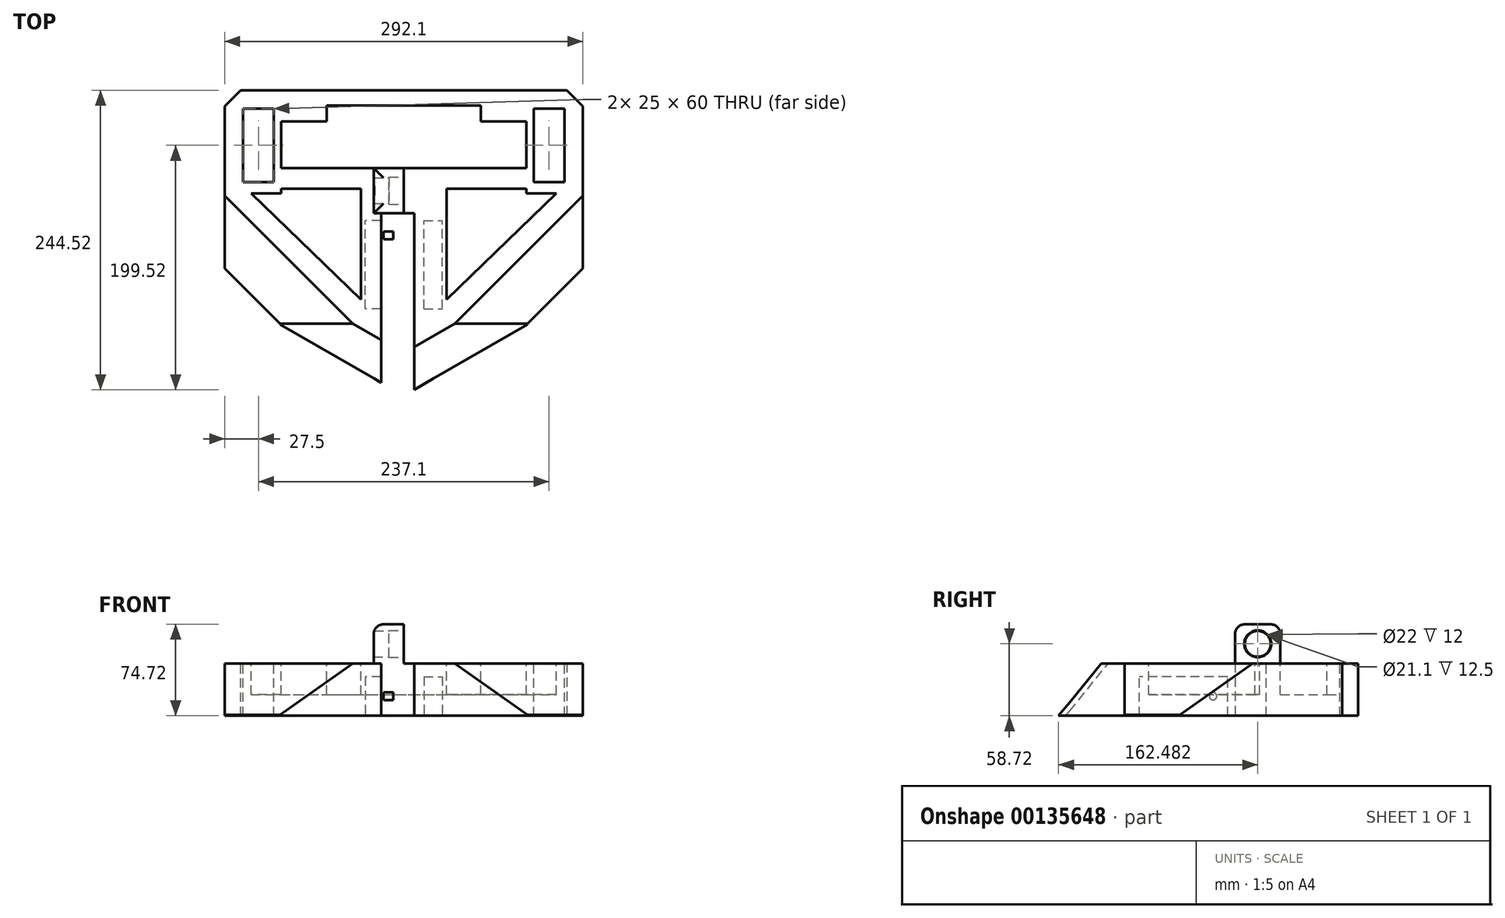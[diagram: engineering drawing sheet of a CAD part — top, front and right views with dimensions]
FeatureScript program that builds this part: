
annotation { "Feature Type Name" : "Feature", "Feature Type Description" : "" }
export const myFeature = defineFeature(function(context is Context, id is Id, definition is map)
    precondition{}
    {
        {
            var Q0;
            Q0=qCreatedBy(makeId("Top.planeOp"),FACE);
            var sketch = newSketch(context, id + "F0", { "sketchPlane" : qUnion([Q0])});
            skLineSegment(sketch, "E0.bottom", {"start": v(-146.05, -95.25) * mm, "end": v(146.05, -95.25) * mm});
            skLineSegment(sketch, "E0.top", {"start": v(-146.05, 95.25) * mm, "end": v(146.05, 95.25) * mm});
            skLineSegment(sketch, "E0.left", {"start": v(-146.05, -95.25) * mm, "end": v(-146.05, 95.25) * mm});
            skLineSegment(sketch, "E0.right", {"start": v(146.05, -95.25) * mm, "end": v(146.05, 95.25) * mm});
            skPoint(sketch, "E0.middle", {"position": v(0, 0) * mm});
            skLineSegment(sketch, "E1", {"start": v(0, -95.25) * mm, "end": v(0, 95.25) * mm, "construction": true});
            skLineSegment(sketch, "E2", {"start": v(0, -5.25) * mm, "end": v(-8.5, -5.25) * mm});
            skLineSegment(sketch, "E3", {"start": v(-8.5, -5.25) * mm, "end": v(-8.5, -95.25) * mm});
            skLineSegment(sketch, "E4.MirrorCS", {"start": v(0, -5.25) * mm, "end": v(8.5, -5.25) * mm});
            skLineSegment(sketch, "E5.MirrorCS", {"start": v(8.5, -5.25) * mm, "end": v(8.5, -95.25) * mm});
            skSolve(sketch);
        }
        {
            var Q0;
            Q0=makeQuery(id+"F0.imprint","IMPRINT",FACE,{"disambiguationData":[TD([[makeQuery(id+"F0.imprint","IMPRINT",EDGE,{"derivedFrom":sQuery(id+"F0.wireOp",EDGE,"E0.bottom")}),1.0]])]});
            extrude(context, id + "F1", {"entities" : qUnion([Q0]), "depth" : 42.72 * mm});
        }
        {
            var Q0;
            Q0=makeQuery(id+"F1.opExtrude","CAP_FACE",FACE,{"disambiguationData":[OSD([sQuery(id+"F0.wireOp",EDGE,"E0.bottom"),sQuery(id+"F0.wireOp",EDGE,"E0.top"),sQuery(id+"F0.wireOp",EDGE,"E0.left"),sQuery(id+"F0.wireOp",EDGE,"E0.right")])],"isStart":false});
            var sketch = newSketch(context, id + "F2", { "sketchPlane" : qUnion([Q0])});
            skLineSegment(sketch, "E6.bottom", {"start": v(-131.05, 80.25) * mm, "end": v(-106.05, 80.25) * mm});
            skLineSegment(sketch, "E6.top", {"start": v(-131.05, 20.25) * mm, "end": v(-106.05, 20.25) * mm});
            skLineSegment(sketch, "E6.left", {"start": v(-131.05, 80.25) * mm, "end": v(-131.05, 20.25) * mm});
            skLineSegment(sketch, "E6.right", {"start": v(-106.05, 80.25) * mm, "end": v(-106.05, 20.25) * mm});
            skLineSegment(sketch, "E7.MirrorCS", {"start": v(106.05, 80.25) * mm, "end": v(106.05, 20.25) * mm});
            skLineSegment(sketch, "E8.MirrorCS", {"start": v(131.05, 80.25) * mm, "end": v(131.05, 20.25) * mm});
            skLineSegment(sketch, "E9.MirrorCS", {"start": v(131.05, 20.25) * mm, "end": v(106.05, 20.25) * mm});
            skLineSegment(sketch, "E10.MirrorCS", {"start": v(131.05, 80.25) * mm, "end": v(106.05, 80.25) * mm});
            skSolve(sketch);
        }
        {
            var Q0;
            Q0=makeQuery(id+"F2.imprint","IMPRINT",FACE,{"disambiguationData":[TD([[makeQuery(id+"F2.imprint","IMPRINT",EDGE,{"derivedFrom":sQuery(id+"F2.wireOp",EDGE,"E6.bottom")}),-1.0]])]});
            var Q1;
            Q1=makeQuery(id+"F2.imprint","IMPRINT",FACE,{"disambiguationData":[TD([[makeQuery(id+"F2.imprint","IMPRINT",EDGE,{"derivedFrom":sQuery(id+"F2.wireOp",EDGE,"2fe5a682-8a8e-47e5-9a97-2ca4f21bb82e0.MirrorCS")}),1.0]])]});
            var Q2;
            Q2=makeQuery(id+"F2.imprint","IMPRINT",FACE,{"disambiguationData":[TD([[makeQuery(id+"F2.imprint","IMPRINT",EDGE,{"derivedFrom":sQuery(id+"F2.wireOp",EDGE,"E7.MirrorCS")}),1.0]])]});
            extrude(context, id + "F3", {"entities" : qUnion([Q0, Q1, Q2]), "operationType" : NewBodyOperationType.REMOVE, "oppositeDirection" : true, "depth" : 500 * mm});
        }
        {
            var Q0;
            Q0=makeQuery(id+"F1.opExtrude","CAP_FACE",FACE,{"disambiguationData":[OSD([sQuery(id+"F0.wireOp",EDGE,"E0.bottom"),sQuery(id+"F0.wireOp",EDGE,"E0.top"),sQuery(id+"F0.wireOp",EDGE,"E0.left"),sQuery(id+"F0.wireOp",EDGE,"E0.right")])],"isStart":false});
            var sketch = newSketch(context, id + "F4", { "sketchPlane" : qUnion([Q0])});
            skLineSegment(sketch, "E11.bottom", {"start": v(-100.05, 31.67) * mm, "end": v(100.05, 31.67) * mm});
            skLineSegment(sketch, "E11.top", {"start": v(-100.05, 69.67) * mm, "end": v(-62.8, 69.67) * mm});
            skLineSegment(sketch, "E11.left", {"start": v(-100.05, 31.67) * mm, "end": v(-100.05, 69.67) * mm});
            skLineSegment(sketch, "E11.right", {"start": v(100.05, 31.67) * mm, "end": v(100.05, 69.67) * mm});
            skPoint(sketch, "E11.middle", {"position": v(0, 50.67) * mm});
            skLineSegment(sketch, "E12.top", {"start": v(-62.8, 82.87) * mm, "end": v(62.8, 82.87) * mm});
            skLineSegment(sketch, "E12.left", {"start": v(-62.8, 69.67) * mm, "end": v(-62.8, 82.87) * mm});
            skLineSegment(sketch, "E12.right", {"start": v(62.8, 69.67) * mm, "end": v(62.8, 82.87) * mm});
            skPoint(sketch, "E12.middle", {"position": v(0, 69.67) * mm});
            skPoint(sketch, "E12.bottom.start.orphan", {"position": v(-62.8, 56.48) * mm});
            skLineSegment(sketch, "E13.trimOffspring", {"start": v(62.8, 69.67) * mm, "end": v(100.05, 69.67) * mm});
            skPoint(sketch, "E14.orphan", {"position": v(62.8, 56.48) * mm});
            skLineSegment(sketch, "E15", {"start": v(-106.05, 50.25) * mm, "end": v(106.05, 50.67) * mm, "construction": true});
            skPoint(sketch, "E15.endSnap0", {"position": v(-100.05, 50.67) * mm});
            skLineSegment(sketch, "E16", {"start": v(-100.05, 31.67) * mm, "end": v(-100.05, 10.92) * mm});
            skLineSegment(sketch, "E17", {"start": v(-100.05, 10.92) * mm, "end": v(-124.52, 10.92) * mm});
            skLineSegment(sketch, "E18", {"start": v(-124.52, 10.92) * mm, "end": v(-34.99, -75.74) * mm});
            skLineSegment(sketch, "E19", {"start": v(-34.99, -75.74) * mm, "end": v(-34.99, 31.67) * mm});
            skLineSegment(sketch, "E20", {"start": v(-100.05, 14.9) * mm, "end": v(-34.99, 14.9) * mm});
            skLineSegment(sketch, "E21.MirrorCS", {"start": v(100.05, 31.67) * mm, "end": v(100.05, 10.92) * mm});
            skLineSegment(sketch, "E22.MirrorCS", {"start": v(100.05, 10.92) * mm, "end": v(124.52, 10.92) * mm});
            skLineSegment(sketch, "E23.MirrorCS", {"start": v(100.05, 14.9) * mm, "end": v(34.99, 14.9) * mm});
            skLineSegment(sketch, "E24.MirrorCS", {"start": v(34.99, -75.74) * mm, "end": v(34.99, 31.67) * mm});
            skLineSegment(sketch, "E25.MirrorCS", {"start": v(124.52, 10.92) * mm, "end": v(34.99, -75.74) * mm});
            skSolve(sketch);
        }
        {
            var Q0;
            Q0=makeQuery(id+"F4.imprint","IMPRINT",FACE,{"disambiguationData":[TD([[makeQuery(id+"F4.imprint","IMPRINT",EDGE,{"derivedFrom":sQuery(id+"F4.wireOp",EDGE,"a0hWfdY4-Ffop-qyRK-2ZFo-kRXj5DdomlVb.bottom")}),1.0]])]});
            var Q1;
            Q1=makeQuery(id+"F4.imprint","IMPRINT",FACE,{"disambiguationData":[TD([[makeQuery(id+"F4.imprint","IMPRINT",EDGE,{"derivedFrom":sQuery(id+"F4.wireOp",EDGE,"bdf87d20-7c82-468c-9b95-8ea2358493bd0.MirrorCS")}),1.0]])]});
            var Q2;
            Q2=makeQuery(id+"F4.imprint","IMPRINT",FACE,{"disambiguationData":[TD([[makeQuery(id+"F4.imprint","IMPRINT",EDGE,{"derivedFrom":sQuery(id+"F4.wireOp",EDGE,"E11.bottom")}),1.0]])]});
            var Q3;
            {var subQ3=sQuery(id+"F4.wireOp",EDGE,"E17");Q3=makeQuery(id+"F4.imprint","IMPRINT",FACE,{"disambiguationData":[TD([[makeQuery(id+"F4.imprint","IMPRINT",EDGE,{"derivedFrom":subQ3}),1.0]])]});}
            var Q4;
            {var subQ3=sQuery(id+"F4.wireOp",EDGE,"E22.MirrorCS");Q4=makeQuery(id+"F4.imprint","IMPRINT",FACE,{"disambiguationData":[TD([[makeQuery(id+"F4.imprint","IMPRINT",EDGE,{"derivedFrom":subQ3}),-1.0]])]});}
            extrude(context, id + "F5", {"entities" : qUnion([Q0, Q1, Q2, Q3, Q4]), "operationType" : NewBodyOperationType.REMOVE, "oppositeDirection" : true, "depth" : 25.4 * mm});
        }
        {
            var Q0;
            Q0=makeQuery(id+"F1.opExtrude","SWEPT_EDGE",EDGE,{"disambiguationData":[OSD([sQuery(id+"F0.wireOp",EDGE,"E0.top"),sQuery(id+"F0.wireOp",EDGE,"E0.left")])]});
            var Q1;
            Q1=makeQuery(id+"F1.opExtrude","SWEPT_EDGE",EDGE,{"disambiguationData":[OSD([sQuery(id+"F0.wireOp",EDGE,"E0.top"),sQuery(id+"F0.wireOp",EDGE,"E0.right")])]});
            chamfer(context, id + "F6", {"entities" : qUnion([Q0, Q1]), "width" : 13 * mm, "tangentPropagation" : true});
        }
        {
            var Q0;
            Q0=makeQuery(id+"F1.opExtrude","SWEPT_EDGE",EDGE,{"disambiguationData":[OSD([sQuery(id+"F0.wireOp",EDGE,"E0.bottom"),sQuery(id+"F0.wireOp",EDGE,"E0.left")])]});
            var Q1;
            Q1=makeQuery(id+"F1.opExtrude","SWEPT_EDGE",EDGE,{"disambiguationData":[OSD([sQuery(id+"F0.wireOp",EDGE,"E0.bottom"),sQuery(id+"F0.wireOp",EDGE,"E0.right")])]});
            chamfer(context, id + "F7", {"entities" : qUnion([Q0, Q1]), "width" : 45 * mm, "tangentPropagation" : true});
        }
        {
            var Q0;
            {var subQ0=sQuery(id+"F0.wireOp",EDGE,"E0.left");var subQ1=sQuery(id+"F0.wireOp",EDGE,"E0.bottom");Q0=makeQuery(id+"F7.opChamfer","BLEND_EDGE",EDGE,{"blendedFrom":[makeQuery(id+"F1.opExtrude","SWEPT_EDGE",EDGE,{"disambiguationData":[OSD([subQ1,subQ0])]}),makeQuery(id+"F1.opExtrude","CAP_FACE",FACE,{"disambiguationData":[OSD([subQ1,sQuery(id+"F0.wireOp",EDGE,"E0.top"),subQ0,sQuery(id+"F0.wireOp",EDGE,"E0.right"),sQuery(id+"F0.wireOp",EDGE,"E2"),sQuery(id+"F0.wireOp",EDGE,"E3"),sQuery(id+"F0.wireOp",EDGE,"E4.MirrorCS"),sQuery(id+"F0.wireOp",EDGE,"E5.MirrorCS")])],"isStart":false})],"blendedInto":[makeQuery(id+"F1.opExtrude","CAP_FACE",FACE,{"disambiguationData":[OSD([subQ1,sQuery(id+"F0.wireOp",EDGE,"E0.top"),subQ0,sQuery(id+"F0.wireOp",EDGE,"E0.right"),sQuery(id+"F0.wireOp",EDGE,"E2"),sQuery(id+"F0.wireOp",EDGE,"E3"),sQuery(id+"F0.wireOp",EDGE,"E4.MirrorCS"),sQuery(id+"F0.wireOp",EDGE,"E5.MirrorCS")])],"isStart":false})]});}
            var Q1;
            {var subQ0=sQuery(id+"F0.wireOp",EDGE,"E0.right");var subQ1=sQuery(id+"F0.wireOp",EDGE,"E0.bottom");Q1=makeQuery(id+"F7.opChamfer","BLEND_EDGE",EDGE,{"blendedFrom":[makeQuery(id+"F1.opExtrude","SWEPT_EDGE",EDGE,{"disambiguationData":[OSD([subQ1,subQ0])]}),makeQuery(id+"F1.opExtrude","CAP_FACE",FACE,{"disambiguationData":[OSD([subQ1,sQuery(id+"F0.wireOp",EDGE,"E0.top"),sQuery(id+"F0.wireOp",EDGE,"E0.left"),subQ0,sQuery(id+"F0.wireOp",EDGE,"E2"),sQuery(id+"F0.wireOp",EDGE,"E3"),sQuery(id+"F0.wireOp",EDGE,"E4.MirrorCS"),sQuery(id+"F0.wireOp",EDGE,"E5.MirrorCS")])],"isStart":false})],"blendedInto":[makeQuery(id+"F1.opExtrude","CAP_FACE",FACE,{"disambiguationData":[OSD([subQ1,sQuery(id+"F0.wireOp",EDGE,"E0.top"),sQuery(id+"F0.wireOp",EDGE,"E0.left"),subQ0,sQuery(id+"F0.wireOp",EDGE,"E2"),sQuery(id+"F0.wireOp",EDGE,"E3"),sQuery(id+"F0.wireOp",EDGE,"E4.MirrorCS"),sQuery(id+"F0.wireOp",EDGE,"E5.MirrorCS")])],"isStart":false})]});}
            chamfer(context, id + "F8", {"entities" : qUnion([Q0, Q1]), "width" : 42 * mm, "tangentPropagation" : true});
        }
        {
            var Q0;
            Q0=makeQuery(id+"F1.opExtrude","CAP_FACE",FACE,{"disambiguationData":[OSD([sQuery(id+"F0.wireOp",EDGE,"E0.bottom"),sQuery(id+"F0.wireOp",EDGE,"E0.top"),sQuery(id+"F0.wireOp",EDGE,"E0.left"),sQuery(id+"F0.wireOp",EDGE,"E0.right"),sQuery(id+"F0.wireOp",EDGE,"E2"),sQuery(id+"F0.wireOp",EDGE,"E3"),sQuery(id+"F0.wireOp",EDGE,"E4.MirrorCS"),sQuery(id+"F0.wireOp",EDGE,"E5.MirrorCS")])],"isStart":true});
            var sketch = newSketch(context, id + "F9", { "sketchPlane" : qUnion([Q0])});
            skLineSegment(sketch, "E26.bottom", {"start": v(-16.5, 83.25) * mm, "end": v(-31.5, 83.25) * mm});
            skLineSegment(sketch, "E26.top", {"start": v(-16.5, 11.3) * mm, "end": v(-31.5, 11.3) * mm});
            skLineSegment(sketch, "E26.left", {"start": v(-16.5, 83.25) * mm, "end": v(-16.5, 11.3) * mm});
            skLineSegment(sketch, "E26.right", {"start": v(-31.5, 83.25) * mm, "end": v(-31.5, 11.3) * mm});
            skLineSegment(sketch, "E27.MirrorCS", {"start": v(16.5, 83.25) * mm, "end": v(16.5, 11.3) * mm});
            skLineSegment(sketch, "E28.MirrorCS", {"start": v(16.5, 83.25) * mm, "end": v(31.5, 83.25) * mm});
            skLineSegment(sketch, "E29.MirrorCS", {"start": v(31.5, 83.25) * mm, "end": v(31.5, 11.3) * mm});
            skLineSegment(sketch, "E30.MirrorCS", {"start": v(16.5, 11.3) * mm, "end": v(31.5, 11.3) * mm});
            skSolve(sketch);
        }
        {
            var Q0;
            Q0=makeQuery(id+"F9.imprint","IMPRINT",FACE,{"disambiguationData":[TD([[makeQuery(id+"F9.imprint","IMPRINT",EDGE,{"derivedFrom":sQuery(id+"F9.wireOp",EDGE,"E26.bottom")}),1.0]])]});
            var Q1;
            Q1=makeQuery(id+"F9.imprint","IMPRINT",FACE,{"disambiguationData":[TD([[makeQuery(id+"F9.imprint","IMPRINT",EDGE,{"derivedFrom":sQuery(id+"F9.wireOp",EDGE,"E27.MirrorCS")}),1.0]])]});
            extrude(context, id + "F10", {"entities" : qUnion([Q0, Q1]), "operationType" : NewBodyOperationType.REMOVE, "oppositeDirection" : true, "depth" : 32 * mm});
        }
        {
            var Q0;
            Q0=makeQuery(id+"F1.opExtrude","SWEPT_FACE",FACE,{"disambiguationData":[OSD([sQuery(id+"F0.wireOp",EDGE,"E3")])]});
            var sketch = newSketch(context, id + "F11", { "sketchPlane" : qUnion([Q0])});
            skPoint(sketch, "E31.endSnap0", {"position": v(-5.25, 21.36) * mm});
            skCircle(sketch, "E32", {"center": v(-77.25, 16) * mm, "radius": 3.05 * mm});
            skLineSegment(sketch, "E33", {"start": v(-50.25, 0) * mm, "end": v(-50.25, 42.72) * mm, "construction": true});
            skCircle(sketch, "E34.MirrorC", {"center": v(-23.25, 16) * mm, "radius": 3.05 * mm});
            skLineSegment(sketch, "E35", {"start": v(-77.25, 16) * mm, "end": v(-23.25, 16) * mm, "construction": true});
            skCircle(sketch, "E36", {"center": v(-50.25, 16) * mm, "radius": 3.05 * mm});
            skSolve(sketch);
        }
        {
            var Q0;
            Q0=makeQuery(id+"F11.imprint","IMPRINT",FACE,{"disambiguationData":[TD([[makeQuery(id+"F11.imprint","IMPRINT",EDGE,{"derivedFrom":sQuery(id+"F11.wireOp",EDGE,"E32")}),1.0]])]});
            var Q1;
            Q1=makeQuery(id+"F11.imprint","IMPRINT",FACE,{"disambiguationData":[TD([[makeQuery(id+"F11.imprint","IMPRINT",EDGE,{"derivedFrom":sQuery(id+"F11.wireOp",EDGE,"E34.MirrorC")}),-1.0]])]});
            var Q2;
            Q2=makeQuery(id+"F11.imprint","IMPRINT",FACE,{"disambiguationData":[TD([[makeQuery(id+"F11.imprint","IMPRINT",EDGE,{"derivedFrom":sQuery(id+"F11.wireOp",EDGE,"E36")}),1.0]])]});
            extrude(context, id + "F12", {"entities" : qUnion([Q0, Q1, Q2]), "operationType" : NewBodyOperationType.REMOVE, "oppositeDirection" : true, "depth" : 10 * mm});
        }
        {
            var Q0;
            {var subQ0=sQuery(id+"F0.wireOp",EDGE,"E0.bottom");Q0=makeQuery(id+"F1.opExtrude","SWEPT_FACE",FACE,{"disambiguationData":[OSD([subQ0]),TDD([makeQuery(id+"F0.imprint","IMPRINT",EDGE,{"disambiguationData":[TD([[makeQuery(id+"F0.imprint","INTERSECT",VERTEX,{"derivedFrom":[subQ0,sQuery(id+"F0.wireOp",EDGE,"E0.right")]}),1.0]])],"derivedFrom":subQ0})])]});}
            var sketch = newSketch(context, id + "F13", { "sketchPlane" : qUnion([Q0])});
            skLineSegment(sketch, "E37", {"start": v(8.5, 42.72) * mm, "end": v(8.5, 0) * mm});
            skLineSegment(sketch, "E38", {"start": v(8.5, 0) * mm, "end": v(101.05, 0) * mm});
            skLineSegment(sketch, "E39", {"start": v(41.65, 42.72) * mm, "end": v(8.5, 42.72) * mm});
            skLineSegment(sketch, "E40", {"start": v(41.65, 42.72) * mm, "end": v(101.05, 0.72) * mm});
            skLineSegment(sketch, "E41", {"start": v(101.05, 0.72) * mm, "end": v(101.05, 0) * mm});
            skSolve(sketch);
        }
        {
            var Q0;
            Q0=makeQuery(id+"F13.imprint","IMPRINT",FACE,{"disambiguationData":[TD([[makeQuery(id+"F13.imprint","IMPRINT",EDGE,{"derivedFrom":sQuery(id+"F13.wireOp",EDGE,"E37")}),1.0]])]});
            var Q1;
            {var subQ0=sQuery(id+"F0.wireOp",EDGE,"E0.bottom");Q1=makeQuery(id+"F1.opExtrude","SWEPT_FACE",FACE,{"disambiguationData":[OSD([subQ0]),TDD([makeQuery(id+"F0.imprint","IMPRINT",EDGE,{"disambiguationData":[TD([[makeQuery(id+"F0.imprint","INTERSECT",VERTEX,{"derivedFrom":[subQ0,sQuery(id+"F0.wireOp",EDGE,"E0.left")]}),-1.0]])],"derivedFrom":subQ0})])]});}
            extrude(context, id + "F14", {"entities" : qUnion([Q0, Q1]), "operationType" : NewBodyOperationType.ADD, "depth" : 45 * mm});
        }
        {
            var Q0;
            Q0=makeQuery(id+"F14.opExtrude","CAP_EDGE",EDGE,{"disambiguationData":[OSD([sQuery(id+"F13.wireOp",EDGE,"E40")])],"isStart":false});
            var Q1;
            Q1=makeQuery(id+"F14.opExtrude","CAP_EDGE",EDGE,{"disambiguationData":[OSD([sQuery(id+"F0.wireOp",EDGE,"E0.bottom"),sQuery(id+"F0.wireOp",EDGE,"E0.top"),sQuery(id+"F0.wireOp",EDGE,"E0.left"),sQuery(id+"F0.wireOp",EDGE,"E0.right"),sQuery(id+"F0.wireOp",EDGE,"E2"),sQuery(id+"F0.wireOp",EDGE,"E3"),sQuery(id+"F0.wireOp",EDGE,"E4.MirrorCS"),sQuery(id+"F0.wireOp",EDGE,"E5.MirrorCS")])],"isStart":false});
            chamfer(context, id + "F15", {"entities" : qUnion([Q0, Q1]), "width" : 45 * mm, "tangentPropagation" : true});
        }
        {
            var Q0;
            Q0=makeQuery(id+"F14.opExtrude","CAP_FACE",FACE,{"disambiguationData":[OSD([sQuery(id+"F13.wireOp",EDGE,"E37"),sQuery(id+"F13.wireOp",EDGE,"E38"),sQuery(id+"F13.wireOp",EDGE,"E39"),sQuery(id+"F13.wireOp",EDGE,"E40"),sQuery(id+"F13.wireOp",EDGE,"E41")])],"isStart":false});
            var Q1;
            Q1=makeQuery(id+"F14.opExtrude","CAP_FACE",FACE,{"disambiguationData":[OSD([sQuery(id+"F0.wireOp",EDGE,"E0.bottom")])],"isStart":false});
            extrude(context, id + "F16", {"entities" : qUnion([Q0, Q1]), "operationType" : NewBodyOperationType.ADD, "depth" : 10 * mm});
        }
        {
            var Q0;
            Q0=makeQuery(id+"F16.opExtrude","CAP_EDGE",EDGE,{"disambiguationData":[OSD([sQuery(id+"F13.wireOp",EDGE,"E37"),sQuery(id+"F13.wireOp",EDGE,"E38"),sQuery(id+"F13.wireOp",EDGE,"E39"),sQuery(id+"F13.wireOp",EDGE,"E40"),sQuery(id+"F13.wireOp",EDGE,"E41")])],"isStart":false});
            var Q1;
            Q1=makeQuery(id+"F16.opExtrude","CAP_EDGE",EDGE,{"disambiguationData":[OSD([sQuery(id+"F0.wireOp",EDGE,"E0.bottom"),sQuery(id+"F0.wireOp",EDGE,"E0.top"),sQuery(id+"F0.wireOp",EDGE,"E0.left"),sQuery(id+"F0.wireOp",EDGE,"E0.right"),sQuery(id+"F0.wireOp",EDGE,"E2"),sQuery(id+"F0.wireOp",EDGE,"E3"),sQuery(id+"F0.wireOp",EDGE,"E4.MirrorCS"),sQuery(id+"F0.wireOp",EDGE,"E5.MirrorCS")])],"isStart":false});
            chamfer(context, id + "F17", {"entities" : qUnion([Q0, Q1]), "width" : 10 * mm, "tangentPropagation" : true});
        }
        {
            var Q0;
            Q0=makeQuery(id+"F1.opExtrude","CAP_FACE",FACE,{"disambiguationData":[OSD([sQuery(id+"F0.wireOp",EDGE,"E0.bottom"),sQuery(id+"F0.wireOp",EDGE,"E0.top"),sQuery(id+"F0.wireOp",EDGE,"E0.left"),sQuery(id+"F0.wireOp",EDGE,"E0.right"),sQuery(id+"F0.wireOp",EDGE,"E2"),sQuery(id+"F0.wireOp",EDGE,"E3"),sQuery(id+"F0.wireOp",EDGE,"E4.MirrorCS"),sQuery(id+"F0.wireOp",EDGE,"E5.MirrorCS")])],"isStart":false});
            var sketch = newSketch(context, id + "F18", { "sketchPlane" : qUnion([Q0])});
            skLineSegment(sketch, "E42", {"start": v(-133.05, 95.25) * mm, "end": v(-146.05, 82.25) * mm});
            skLineSegment(sketch, "E43", {"start": v(-146.05, 82.25) * mm, "end": v(-146.05, 9.15) * mm});
            skLineSegment(sketch, "E44", {"start": v(-146.05, 9.15) * mm, "end": v(-41.65, -95.25) * mm});
            skLineSegment(sketch, "E45", {"start": v(-8.5, -5.25) * mm, "end": v(8.5, -5.25) * mm});
            skLineSegment(sketch, "E46", {"start": v(41.65, -95.25) * mm, "end": v(146.05, 9.15) * mm});
            skLineSegment(sketch, "E47", {"start": v(146.05, 9.15) * mm, "end": v(146.05, 82.25) * mm});
            skLineSegment(sketch, "E48", {"start": v(146.05, 82.25) * mm, "end": v(133.05, 95.25) * mm});
            skLineSegment(sketch, "E49", {"start": v(133.05, 95.25) * mm, "end": v(-133.05, 95.25) * mm});
            skLineSegment(sketch, "E50.bottom", {"start": v(-131.05, 80.25) * mm, "end": v(-106.05, 80.25) * mm});
            skLineSegment(sketch, "E50.top", {"start": v(-131.05, 20.25) * mm, "end": v(-106.05, 20.25) * mm});
            skLineSegment(sketch, "E50.left", {"start": v(-131.05, 80.25) * mm, "end": v(-131.05, 20.25) * mm});
            skLineSegment(sketch, "E50.right", {"start": v(-106.05, 80.25) * mm, "end": v(-106.05, 20.25) * mm});
            skLineSegment(sketch, "E51.bottom", {"start": v(106.05, 80.25) * mm, "end": v(131.05, 80.25) * mm});
            skLineSegment(sketch, "E51.top", {"start": v(106.05, 20.25) * mm, "end": v(131.05, 20.25) * mm});
            skLineSegment(sketch, "E51.left", {"start": v(106.05, 80.25) * mm, "end": v(106.05, 20.25) * mm});
            skLineSegment(sketch, "E51.right", {"start": v(131.05, 80.25) * mm, "end": v(131.05, 20.25) * mm});
            skLineSegment(sketch, "E52", {"start": v(8.5, -5.25) * mm, "end": v(8.5, -114.4) * mm});
            skLineSegment(sketch, "E53", {"start": v(8.5, -114.4) * mm, "end": v(41.65, -95.25) * mm});
            skLineSegment(sketch, "E54", {"start": v(-8.5, -5.25) * mm, "end": v(-8.5, -114.4) * mm});
            skLineSegment(sketch, "E55", {"start": v(-8.5, -114.4) * mm, "end": v(-41.65, -95.25) * mm});
            skLineSegment(sketch, "E56.bottom", {"start": v(0, 31.67) * mm, "end": v(-24.5, 31.67) * mm});
            skLineSegment(sketch, "E56.top", {"start": v(0, -5.25) * mm, "end": v(-24.5, -5.25) * mm});
            skLineSegment(sketch, "E56.left", {"start": v(0, 31.67) * mm, "end": v(0, -5.25) * mm});
            skLineSegment(sketch, "E56.right", {"start": v(-24.5, 31.67) * mm, "end": v(-24.5, -5.25) * mm});
            skSolve(sketch);
        }
        {
            var Q0;
            Q0=makeQuery(id+"F18.imprint","IMPRINT",FACE,{"disambiguationData":[TD([[makeQuery(id+"F18.imprint","IMPRINT",EDGE,{"derivedFrom":sQuery(id+"F18.wireOp",EDGE,"E56.bottom")}),-1.0]])]});
            extrude(context, id + "F19", {"entities" : qUnion([Q0]), "operationType" : NewBodyOperationType.ADD, "depth" : 32 * mm});
        }
        {
            var Q0;
            Q0=makeQuery(id+"F19.opExtrude","SWEPT_FACE",FACE,{"disambiguationData":[OSD([sQuery(id+"F18.wireOp",EDGE,"E56.left")])]});
            var sketch = newSketch(context, id + "F20", { "sketchPlane" : qUnion([Q0])});
            skLineSegment(sketch, "E57", {"start": v(13.21, 74.72) * mm, "end": v(13.21, 58.72) * mm, "construction": true});
            skCircle(sketch, "E58", {"center": v(13.21, 58.72) * mm, "radius": 11 * mm});
            skSolve(sketch);
        }
        {
            var Q0;
            Q0=makeQuery(id+"F20.imprint","IMPRINT",FACE,{"disambiguationData":[TD([[makeQuery(id+"F20.imprint","IMPRINT",EDGE,{"derivedFrom":sQuery(id+"F20.wireOp",EDGE,"E58")}),1.0]])]});
            extrude(context, id + "F21", {"entities" : qUnion([Q0]), "operationType" : NewBodyOperationType.REMOVE, "oppositeDirection" : true, "depth" : 12 * mm});
        }
        {
            var Q0;
            Q0=makeQuery(id+"F19.opExtrude","CAP_EDGE",EDGE,{"disambiguationData":[OSD([sQuery(id+"F18.wireOp",EDGE,"E56.top")])],"isStart":false});
            var Q1;
            Q1=makeQuery(id+"F19.opExtrude","CAP_EDGE",EDGE,{"disambiguationData":[OSD([sQuery(id+"F18.wireOp",EDGE,"E56.bottom")])],"isStart":false});
            var Q2;
            Q2=makeQuery(id+"F19.opExtrude","CAP_EDGE",EDGE,{"disambiguationData":[OSD([sQuery(id+"F18.wireOp",EDGE,"E56.top")])],"isStart":true});
            var Q3;
            Q3=makeQuery(id+"F19.opExtrude","CAP_EDGE",EDGE,{"disambiguationData":[OSD([sQuery(id+"F18.wireOp",EDGE,"E56.right")])],"isStart":true});
            var Q4;
            Q4=makeQuery(id+"F19.opExtrude","CAP_EDGE",EDGE,{"disambiguationData":[OSD([sQuery(id+"F18.wireOp",EDGE,"E56.left")])],"isStart":true});
            var Q5;
            Q5=makeQuery(id+"F19.opExtrude","CAP_EDGE",EDGE,{"disambiguationData":[OSD([sQuery(id+"F18.wireOp",EDGE,"E56.right")])],"isStart":false});
            fillet(context, id + "F22", {"entities" : qUnion([Q0, Q1, Q2, Q3, Q4, Q5]), "radius" : 8 * mm, "tangentPropagation" : true, "allowEdgeOverflow" : false});
        }
        {
            var Q0;
            Q0=makeQuery(id+"F19.opExtrude","SWEPT_FACE",FACE,{"disambiguationData":[OSD([sQuery(id+"F18.wireOp",EDGE,"E56.left")])]});
            var sketch = newSketch(context, id + "F23", { "sketchPlane" : qUnion([Q0])});
            skCircle(sketch, "E59", {"center": v(13.21, 58.72) * mm, "radius": 10.55 * mm});
            skSolve(sketch);
        }
        {
            var Q0;
            Q0 = qSketchRegion(id + "F23", true);
            extrude(context, id + "F24", {"entities" : qUnion([Q0]), "operationType" : NewBodyOperationType.REMOVE, "oppositeDirection" : true, "depth" : 16 * mm});
        }
        {
            var Q0;
            Q0=makeQuery(id+"F24.boolean.opBoolean","COPY",FACE,{"derivedFrom":makeQuery(id+"F24.opExtrude","CAP_FACE",FACE,{"disambiguationData":[OSD([sQuery(id+"F23.wireOp",EDGE,"E59")])],"isStart":false})});
            var sketch = newSketch(context, id + "F25", { "sketchPlane" : qUnion([Q0])});
            skCircle(sketch, "E60", {"center": v(13.23, 58.72) * mm, "radius": 1.05 * mm});
            skLineSegment(sketch, "E61", {"start": v(13.23, 58.72) * mm, "end": v(21.23, 58.72) * mm, "construction": true});
            skCircle(sketch, "E62", {"center": v(21.23, 58.72) * mm, "radius": 1.57 * mm});
            skCircle(sketch, "E63.MirrorC", {"center": v(5.23, 58.72) * mm, "radius": 1.57 * mm});
            skLineSegment(sketch, "E64", {"start": v(13.23, 58.72) * mm, "end": v(13.23, 64.72) * mm, "construction": true});
            skCircle(sketch, "E65", {"center": v(13.23, 64.72) * mm, "radius": 1.57 * mm});
            skCircle(sketch, "E66.MirrorC", {"center": v(13.23, 52.72) * mm, "radius": 1.57 * mm});
            skSolve(sketch);
        }
        {
            var Q0;
            Q0 = qSketchRegion(id + "F25", true);
            var Q1;
            Q1=makeQuery(id+"F25.imprint","IMPRINT",FACE,{"disambiguationData":[TD([[makeQuery(id+"F25.imprint","IMPRINT",EDGE,{"derivedFrom":sQuery(id+"F25.wireOp",EDGE,"E63.MirrorC")}),-1.0]])]});
            var Q2;
            Q2=makeQuery(id+"F25.imprint","IMPRINT",FACE,{"disambiguationData":[TD([[makeQuery(id+"F25.imprint","IMPRINT",EDGE,{"derivedFrom":sQuery(id+"F25.wireOp",EDGE,"E65")}),1.0]])]});
            extrude(context, id + "F26", {"entities" : qUnion([Q0, Q1, Q2]), "operationType" : NewBodyOperationType.REMOVE, "oppositeDirection" : true, "depth" : 25 * mm});
        }
    });
